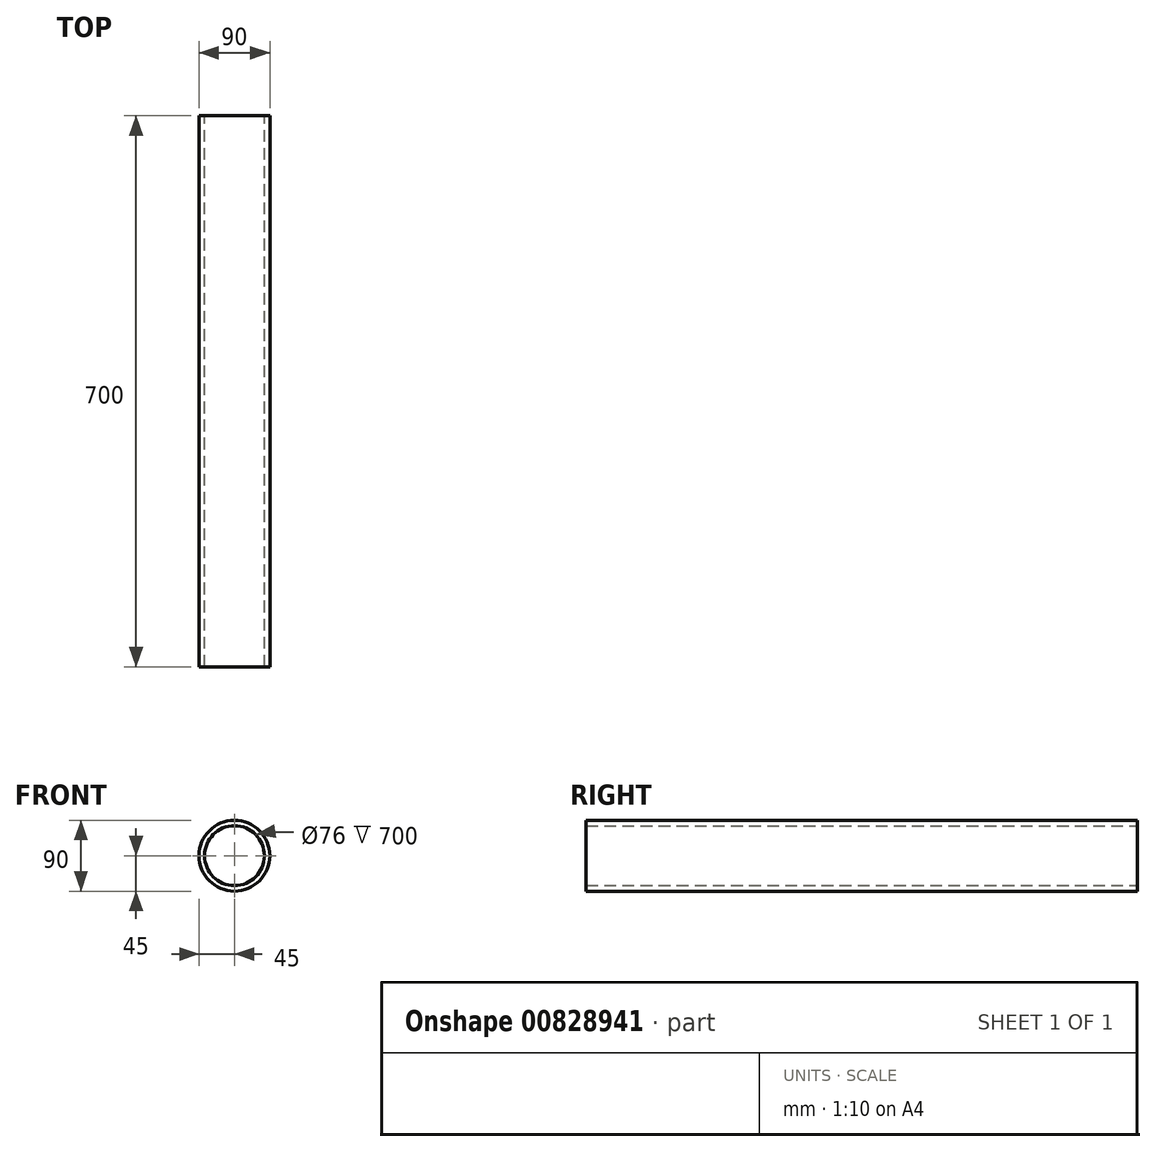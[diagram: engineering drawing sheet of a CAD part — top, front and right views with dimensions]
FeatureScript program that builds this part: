
annotation { "Feature Type Name" : "Feature", "Feature Type Description" : "" }
export const myFeature = defineFeature(function(context is Context, id is Id, definition is map)
    precondition{}
    {
        {
            var Q0;
            Q0=qCreatedBy(makeId("Front.planeOp"),FACE);
            var sketch = newSketch(context, id + "F0", { "sketchPlane" : qUnion([Q0])});
            skCircle(sketch, "E0", {"center": v(0, 0) * mm, "radius": 45 * mm});
            skCircle(sketch, "E1", {"center": v(0, 0) * mm, "radius": 38 * mm});
            skSolve(sketch);
        }
        {
            var Q0;
            Q0=qSketchRegion(id+"F0",true);
            extrude(context, id + "F1", {"entities" : qUnion([Q0]), "depth" : 700 * mm, "offsetDistance" : 25 * mm});
        }
    });
